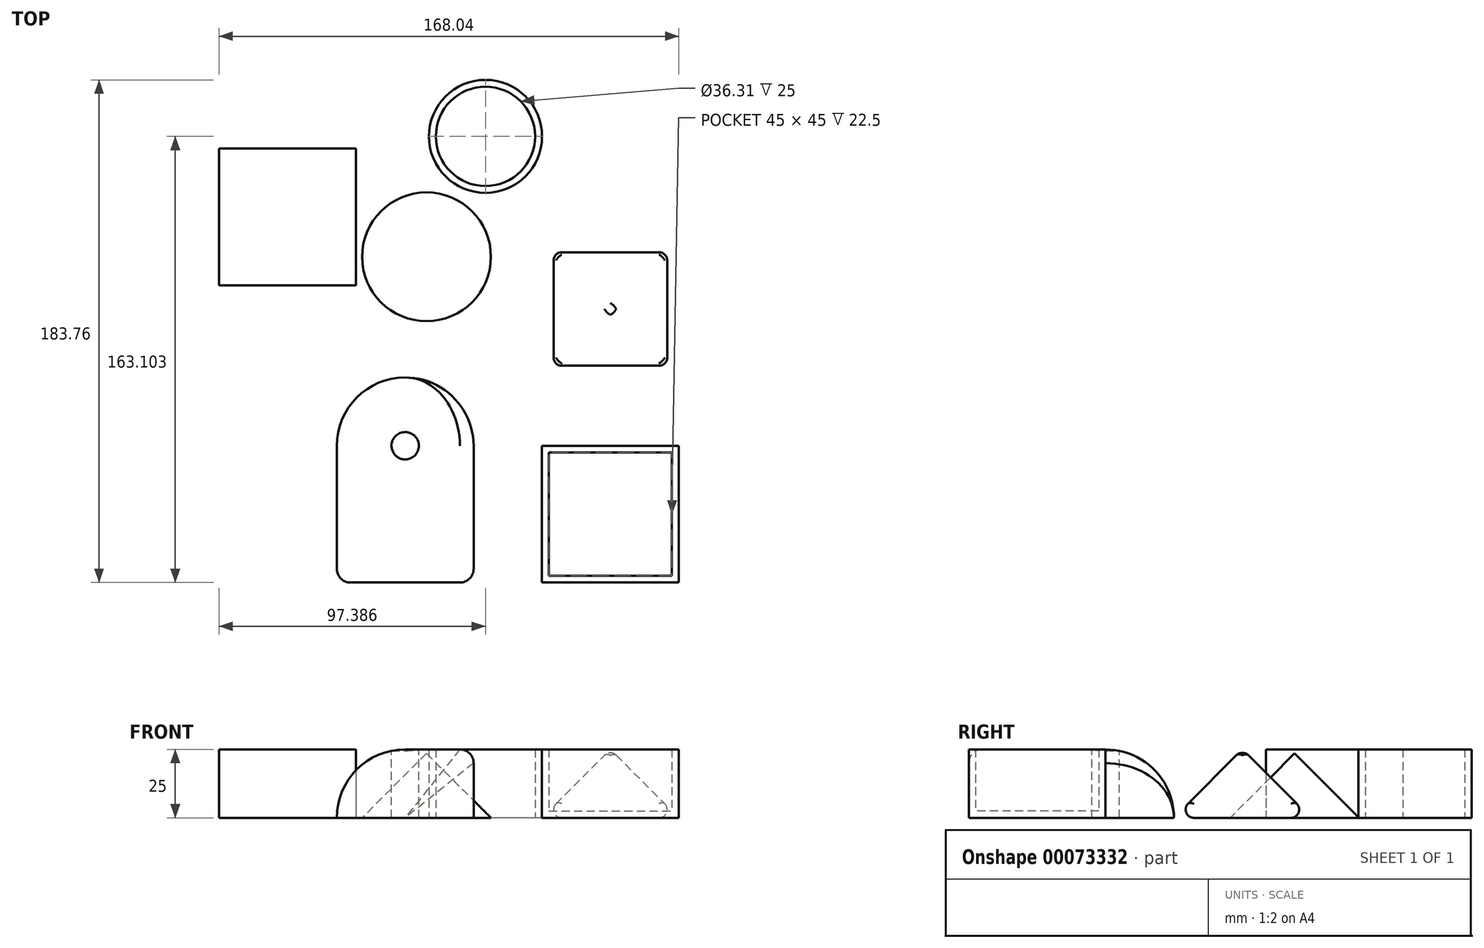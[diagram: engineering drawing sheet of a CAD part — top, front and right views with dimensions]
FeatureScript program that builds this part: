
annotation { "Feature Type Name" : "Feature", "Feature Type Description" : "" }
export const myFeature = defineFeature(function(context is Context, id is Id, definition is map)
    precondition{}
    {
        {
            var Q0;
            Q0=qCreatedBy(makeId("Top.planeOp"),FACE);
            var sketch = newSketch(context, id + "F0", { "sketchPlane" : qUnion([Q0])});
            skPoint(sketch, "E0.rect.middle", {"position": v(0, 0) * mm});
            skLineSegment(sketch, "E1.rect.top", {"start": v(-25, -25) * mm, "end": v(25, -25) * mm});
            skLineSegment(sketch, "E1.rect.left", {"start": v(-25, 25) * mm, "end": v(-25, -25) * mm});
            skLineSegment(sketch, "E1.rect.right", {"start": v(25, 25) * mm, "end": v(25, -25) * mm});
            skPoint(sketch, "E2.rect.middle", {"position": v(75, 0) * mm});
            skLineSegment(sketch, "E3.rect.bottom", {"start": v(50, 25) * mm, "end": v(100, 25) * mm});
            skLineSegment(sketch, "E3.rect.top", {"start": v(50, -25) * mm, "end": v(100, -25) * mm});
            skLineSegment(sketch, "E3.rect.left", {"start": v(50, 25) * mm, "end": v(50, -25) * mm});
            skLineSegment(sketch, "E3.rect.right", {"start": v(100, 25) * mm, "end": v(100, -25) * mm});
            skLineSegment(sketch, "E4.rect.bottom", {"start": v(50, 50) * mm, "end": v(100, 50) * mm});
            skLineSegment(sketch, "E4.rect.top", {"start": v(50, 100) * mm, "end": v(100, 100) * mm});
            skLineSegment(sketch, "E4.rect.left", {"start": v(50, 50) * mm, "end": v(50, 100) * mm});
            skLineSegment(sketch, "E4.rect.right", {"start": v(100, 50) * mm, "end": v(100, 100) * mm});
            skPoint(sketch, "E4.rect.middle", {"position": v(75, 75) * mm});
            skArc(sketch, "E5", {"start": v(25, 25) * mm, "mid": v(0, 50) * mm, "end": v(-25, 25) * mm});
            skLineSegment(sketch, "E6", {"start": v(0, 50) * mm, "end": v(0, -25) * mm});
            skCircle(sketch, "E7", {"center": v(7.79, 94.1) * mm, "radius": 23.55 * mm});
            skCircle(sketch, "E8", {"center": v(29.35, 138.1) * mm, "radius": 20.65 * mm});
            skLineSegment(sketch, "E9.bottom", {"start": v(-68.04, 133.63) * mm, "end": v(-18.04, 133.63) * mm});
            skLineSegment(sketch, "E9.top", {"start": v(-68.04, 83.63) * mm, "end": v(-18.04, 83.63) * mm});
            skLineSegment(sketch, "E9.left", {"start": v(-68.04, 133.63) * mm, "end": v(-68.04, 83.63) * mm});
            skLineSegment(sketch, "E9.right", {"start": v(-18.04, 133.63) * mm, "end": v(-18.04, 83.63) * mm});
            skSolve(sketch);
        }
        {
            var Q0;
            {var subQ0=sQuery(id+"F0.wireOp",EDGE,"E1.rect.right");Q0=makeQuery(id+"F0.imprint","IMPRINT",FACE,{"disambiguationData":[TD([[makeQuery(id+"F0.imprint","IMPRINT",EDGE,{"derivedFrom":subQ0}),-1.0]])]});}
            var Q1;
            Q1=makeQuery(id+"F0.imprint","IMPRINT",FACE,{"disambiguationData":[TD([[makeQuery(id+"F0.imprint","IMPRINT",EDGE,{"derivedFrom":sQuery(id+"F0.wireOp",EDGE,"E3.rect.bottom")}),-1.0]])]});
            extrude(context, id + "F1", {"entities" : qUnion([Q0, Q1]), "depth" : 25 * mm});
        }
        {
            var Q0;
            {var subQ0=sQuery(id+"F0.wireOp",EDGE,"E1.rect.left");Q0=makeQuery(id+"F0.imprint","IMPRINT",FACE,{"disambiguationData":[TD([[makeQuery(id+"F0.imprint","IMPRINT",EDGE,{"derivedFrom":subQ0}),1.0]])]});}
            var Q1;
            Q1=sQuery(id+"F0.wireOp",EDGE,"E6");
            revolve(context, id + "F2", {"operationType" : NewBodyOperationType.ADD, "entities" : qUnion([Q0]), "axis" : qUnion([Q1]), "revolveType" : RevolveType.ONE_DIRECTION, "oppositeDirection" : true, "angle" : 90 * degree});
        }
        {
            var Q0;
            Q0=makeQuery(id+"F1.opExtrude","SWEPT_FACE",FACE,{"disambiguationData":[OSD([sQuery(id+"F0.wireOp",EDGE,"E6")])]});
            extrude(context, id + "F3", {"entities" : qUnion([Q0]), "operationType" : NewBodyOperationType.REMOVE, "oppositeDirection" : true, "depth" : 25 * mm});
        }
        {
            var Q0;
            {var subQ0=sQuery(id+"F0.wireOp",EDGE,"E5");Q0=makeQuery(id+"F3.boolean.opBoolean","INTERSECT",EDGE,{"derivedFrom":[makeQuery(id+"F1.opExtrude","SWEPT_FACE",FACE,{"disambiguationData":[OSD([subQ0])]}),makeQuery(id+"F3.opExtrude","SWEPT_FACE",FACE,{"disambiguationData":[OSD([subQ0])]})]});}
            var Q1;
            Q1=makeQuery(id+"F1.opExtrude","SWEPT_EDGE",EDGE,{"disambiguationData":[OSD([sQuery(id+"F0.wireOp",EDGE,"E1.rect.top"),sQuery(id+"F0.wireOp",EDGE,"E1.rect.right")])]});
            var Q2;
            Q2=makeQuery(id+"F1.opExtrude","CAP_EDGE",EDGE,{"disambiguationData":[OSD([sQuery(id+"F0.wireOp",EDGE,"E1.rect.top")])],"isStart":false});
            fillet(context, id + "F4", {"entities" : qUnion([Q0, Q1, Q2]), "radius" : 5 * mm, "tangentPropagation" : true, "allowEdgeOverflow" : false});
        }
        {
            var Q0;
            Q0=makeQuery(id+"F0.imprint","IMPRINT",FACE,{"disambiguationData":[TD([[makeQuery(id+"F0.imprint","IMPRINT",EDGE,{"derivedFrom":sQuery(id+"F0.wireOp",EDGE,"E4.rect.bottom")}),1.0]])]});
            extrude(context, id + "F5", {"entities" : qUnion([Q0]), "depth" : 50 * mm, "hasDraft" : true, "draftAngle" : 45 * degree, "draftPullDirection" : true});
        }
        {
            var Q0;
            Q0=makeQuery(id+"F5.opExtrude","SWEPT_FACE",FACE,{"disambiguationData":[OSD([sQuery(id+"F0.wireOp",EDGE,"E4.rect.left")])]});
            var Q1;
            Q1=makeQuery(id+"F5.opExtrude","SWEPT_FACE",FACE,{"disambiguationData":[OSD([sQuery(id+"F0.wireOp",EDGE,"E4.rect.bottom")])]});
            var Q2;
            Q2=makeQuery(id+"F5.opExtrude","SWEPT_FACE",FACE,{"disambiguationData":[OSD([sQuery(id+"F0.wireOp",EDGE,"E4.rect.right")])]});
            var Q3;
            Q3=makeQuery(id+"F5.opExtrude","SWEPT_FACE",FACE,{"disambiguationData":[OSD([sQuery(id+"F0.wireOp",EDGE,"E4.rect.top")])]});
            fillet(context, id + "F6", {"entities" : qUnion([Q0, Q1, Q2, Q3]), "radius" : 3 * mm, "tangentPropagation" : true, "allowEdgeOverflow" : false});
        }
        {
            var Q0;
            Q0=makeQuery(id+"F0.imprint","IMPRINT",FACE,{"disambiguationData":[TD([[makeQuery(id+"F0.imprint","IMPRINT",EDGE,{"derivedFrom":sQuery(id+"F0.wireOp",EDGE,"E7")}),1.0]])]});
            extrude(context, id + "F7", {"entities" : qUnion([Q0]), "depth" : 25 * mm, "hasDraft" : true, "draftAngle" : 45 * degree, "draftPullDirection" : true});
        }
        {
            var Q0;
            Q0=makeQuery(id+"F1.opExtrude","CAP_FACE",FACE,{"disambiguationData":[OSD([sQuery(id+"F0.wireOp",EDGE,"E1.rect.top"),sQuery(id+"F0.wireOp",EDGE,"E1.rect.right"),sQuery(id+"F0.wireOp",EDGE,"E5"),sQuery(id+"F0.wireOp",EDGE,"E6")])],"isStart":false});
            var sketch = newSketch(context, id + "F8", { "sketchPlane" : qUnion([Q0])});
            skCircle(sketch, "E10", {"center": v(0, 25) * mm, "radius": 5 * mm});
            skSolve(sketch);
        }
        {
            var Q0;
            {var subQ0=sQuery(id+"F8.wireOp",EDGE,"E10");var subQ1=sQuery(id+"F0.wireOp",EDGE,"E1.rect.left");var subQ2=makeQuery(id+"F3.boolean.opBoolean","COPY",EDGE,{"derivedFrom":makeQuery(id+"F3.opExtrude","SWEPT_EDGE",EDGE,{"disambiguationData":[OSD([subQ1,sQuery(id+"F0.wireOp",EDGE,"E5")])]})});var subQ3=makeQuery(id+"F8.imprint","INTERSECT",VERTEX,{"derivedFrom":[subQ2,subQ0]});Q0=makeQuery(id+"F8.imprint","IMPRINT",FACE,{"disambiguationData":[TD([[makeQuery(id+"F8.imprint","IMPRINT",EDGE,{"disambiguationData":[TD([[subQ3,-1.0]])],"derivedFrom":subQ0}),1.0]])]});}
            var Q1;
            {var subQ0=sQuery(id+"F8.wireOp",EDGE,"E10");var subQ1=sQuery(id+"F0.wireOp",EDGE,"E1.rect.left");var subQ2=makeQuery(id+"F3.boolean.opBoolean","COPY",EDGE,{"derivedFrom":makeQuery(id+"F3.opExtrude","SWEPT_EDGE",EDGE,{"disambiguationData":[OSD([subQ1,sQuery(id+"F0.wireOp",EDGE,"E5")])]})});var subQ3=makeQuery(id+"F8.imprint","INTERSECT",VERTEX,{"derivedFrom":[subQ2,subQ0]});Q1=makeQuery(id+"F8.imprint","IMPRINT",FACE,{"disambiguationData":[TD([[makeQuery(id+"F8.imprint","IMPRINT",EDGE,{"disambiguationData":[TD([[subQ3,1.0]])],"derivedFrom":subQ0}),1.0]])]});}
            extrude(context, id + "F9", {"entities" : qUnion([Q0, Q1]), "operationType" : NewBodyOperationType.REMOVE, "oppositeDirection" : true, "depth" : 25 * mm});
        }
        {
            var Q0;
            Q0=makeQuery(id+"F0.imprint","IMPRINT",FACE,{"disambiguationData":[TD([[makeQuery(id+"F0.imprint","IMPRINT",EDGE,{"derivedFrom":sQuery(id+"F0.wireOp",EDGE,"E8")}),1.0]])]});
            extrude(context, id + "F10", {"entities" : qUnion([Q0]), "depth" : 25 * mm});
        }
        {
            var Q0;
            Q0=makeQuery(id+"F10.opExtrude","CAP_FACE",FACE,{"disambiguationData":[OSD([sQuery(id+"F0.wireOp",EDGE,"E8")])],"isStart":false});
            shell(context, id + "F11", {"entities" : qUnion([Q0]), "thickness" : 2.5 * mm});
        }
        {
            var Q0;
            {var subQ0=sQuery(id+"F0.wireOp",EDGE,"E8");Q0=makeQuery(id+"F11.opShell","OFFSET_FACE",FACE,{"disambiguationData":[OSD([subQ0]),TDD([makeQuery(id+"F10.opExtrude","CAP_FACE",FACE,{"disambiguationData":[OSD([subQ0])],"isStart":true})])]});}
            extrude(context, id + "F12", {"entities" : qUnion([Q0]), "operationType" : NewBodyOperationType.REMOVE, "oppositeDirection" : true, "depth" : 25 * mm});
        }
        {
            var Q0;
            Q0=makeQuery(id+"F0.imprint","IMPRINT",FACE,{"disambiguationData":[TD([[makeQuery(id+"F0.imprint","IMPRINT",EDGE,{"derivedFrom":sQuery(id+"F0.wireOp",EDGE,"E9.bottom")}),-1.0]])]});
            extrude(context, id + "F13", {"entities" : qUnion([Q0]), "depth" : 25 * mm});
        }
        {
            var Q0;
            Q0=makeQuery(id+"F1.opExtrude","CAP_FACE",FACE,{"disambiguationData":[OSD([sQuery(id+"F0.wireOp",EDGE,"E3.rect.bottom"),sQuery(id+"F0.wireOp",EDGE,"E3.rect.top"),sQuery(id+"F0.wireOp",EDGE,"E3.rect.left"),sQuery(id+"F0.wireOp",EDGE,"E3.rect.right")])],"isStart":false});
            shell(context, id + "F14", {"entities" : qUnion([Q0]), "thickness" : 2.5 * mm});
        }
    });
